# Revit family: QF_BPRO_HAU-PS 5x7_572556
name_source: partatom
category: Sonderausstattung
revit_build: Autodesk Revit 2018 (Build: 20190510_1515(x64)
units: mm (PartAtom-declared; Revit-internal decimal feet)

## family parameters
Arbeitsebenenbasiert = Nein
Beim Laden mit Abzugskörper schneiden = Nein
Bemaßung runder Anschluss = Durchmesser verwenden
Gemeinsam genutzt = Nein
Immer vertikal = Ja
Raumberechnungspunkt = Nein
Teiletyp = Normal

## types (1)
- HAU-PS 5x7
    Artikel Nummer = 572556
    Beschreibung = Handwasch- und Ausgussbecken-Kombination auf Füßen stehend, mit
abnehmbarer Serviceblende,
komplett mit 1 Mischbatterie 1/2" und einer sensorgesteuerten
Mischbatterie und Ablaufgarnitur
Maße: Handwaschbecken: 340 x 240 x 150 mm
Ausgussbecken: 370 x 340 x 150
    Beschreibung durch Hersteller analog Leistungsverzeichniskurztext = Abmessungen:

Länge:   	500 mm
Breite:  	700 mm
Höhe:          900/560 mm

Beckengröße:
Länge:   	340 mm
Breite:  	240 mm
Höhe:    	150 mm

Länge:   	370 mm
Breite:  	340 mm
Höhe:    	150 mm


Ausführung:

Handwasch- und Ausgussbecken sind aus platzsparenden Gründen übereinander angeordnet. Bestehend aus einer kompakten, selbsttragenden Bauweise, auf vier längsnahtgeschweißten Vierkantrohrfüßen (je 40x40x1,25 mm) stehend. Die Steherenden sind zum Ausgleich von Bodenunebenheiten mit höhenverstellbaren Kunststoffschraubstollen (+/- 15 mm) ausgestattet. 

Beide Becken sind mit dreiseitigen CNS-Blenden versehen, wobei die schräg angeordnete Verkleidung des Waschbeckens abnehmbar ist. Die Becken sind im Einstückverfahren tiefgezogen und naht- und fugenlos in die Abdeckung eingeschweißt. Die Abdeckungen sind dreiseitig 50 mm abgekantet. Das Handwaschbecken ist hinten 50 mm aufgekantet mit Umschlag nach außen. Das Ausgussbecken ist umlaufend mit einem erhöhten Profilrand (Schwallrand) versehen.

Die Handwasch-Ausgussbecken-Kombination ist mit Stopfen-Überlaufventilen 1 1/2" und mit einem Auflagerost aus stabilem Kunststoff (Material: ASA) ausgestattet. Das Handwaschbecken ist mit einer berührungslosen Armatur 1/2" (Modell Aquis) versehen. Die Temperatur ist mittels seitlich angeordnetem Hebel individuell von kalt bis warm einstellbar. Sobald die Hände unter die Armatur gehalten werden, fließt automatisch das Wasser in der vorgewählten Temperatur, bei Wegziehen stoppt der Wasserfluss automatisch. Der Trafo wird im Unterbereich mit Netzanschluss von 230 V/ 50 HZ und entsprechendem Anschlußkabel eingebaut. 
Die manuell regelbare Einhebel-Mischbatterie 1/2" für das Ausgussbecken ist ebenfalls zur Montage auf dem Handwaschbecken vorgesehen.
Die Ver- und Entsorgungsleitungen sowie die Armaturen sind lose beigefügt und können problem-los mittels einer Bedienungs- und Montageanleitung installiert werden. 


Zubehör/ Optionen:

<unrecoverable-encoding: 3 bytes ef82a7>	Abfallschublade:
Die Abfallschublade ist für alle Modelle HAU-P und 
HAU-PS erhältlich. Sie ist unterhalb des 
Ausgussbeckens platziert und lässt sich per Fuß 
öffnen und schließen. Als Abfallbehälter dient ein 
B.PRO
    Beschreibung durch Hersteller analog Leistungsverzeichnislangtext = Abmessungen:

Länge:   	500 mm
Breite:  	700 mm
Höhe:          900/560 mm

Beckengröße:
Länge:   	340 mm
Breite:  	240 mm
Höhe:    	150 mm

Länge:   	370 mm
Breite:  	340 mm
Höhe:    	150 mm


Ausführung:

Handwasch- und Ausgussbecken sind aus platzsparenden Gründen übereinander angeordnet. Bestehend aus einer kompakten, selbsttragenden Bauweise, auf vier längsnahtgeschweißten Vierkantrohrfüßen (je 40x40x1,25 mm) stehend. Die Steherenden sind zum Ausgleich von Bodenunebenheiten mit höhenverstellbaren Kunststoffschraubstollen (+/- 15 mm) ausgestattet. 

Beide Becken sind mit dreiseitigen CNS-Blenden versehen, wobei die schräg angeordnete Verkleidung des Waschbeckens abnehmbar ist. Die Becken sind im Einstückverfahren tiefgezogen und naht- und fugenlos in die Abdeckung eingeschweißt. Die Abdeckungen sind dreiseitig 50 mm abgekantet. Das Handwaschbecken ist hinten 50 mm aufgekantet mit Umschlag nach außen. Das Ausgussbecken ist umlaufend mit einem erhöhten Profilrand (Schwallrand) versehen.

Die Handwasch-Ausgussbecken-Kombination ist mit Stopfen-Überlaufventilen 1 1/2" und mit einem Auflagerost aus stabilem Kunststoff (Material: ASA) ausgestattet. Das Handwaschbecken ist mit einer berührungslosen Armatur 1/2" (Modell Aquis) versehen. Die Temperatur ist mittels seitlich angeordnetem Hebel individuell von kalt bis warm einstellbar. Sobald die Hände unter die Armatur gehalten werden, fließt automatisch das Wasser in der vorgewählten Temperatur, bei Wegziehen stoppt der Wasserfluss automatisch. Der Trafo wird im Unterbereich mit Netzanschluss von 230 V/ 50 HZ und entsprechendem Anschlußkabel eingebaut. 
Die manuell regelbare Einhebel-Mischbatterie 1/2" für das Ausgussbecken ist ebenfalls zur Montage auf dem Handwaschbecken vorgesehen.
Die Ver- und Entsorgungsleitungen sowie die Armaturen sind lose beigefügt und können problem-los mittels einer Bedienungs- und Montageanleitung installiert werden. 


Zubehör/ Optionen:

<unrecoverable-encoding: 3 bytes ef82a7>	Abfallschublade:
Die Abfallschublade ist für alle Modelle HAU-P und 
HAU-PS erhältlich. Sie ist unterhalb des 
Ausgussbeckens platziert und lässt sich per Fuß 
öffnen und schließen. Als Abfallbehälter dient ein 
B.PRO
    Breite Becken unten Strg = 339 mm
    Frequenz = 50 Hz
    Gerätegewicht Netto = 23.00 kg
    Großküchengerätezuordnung = Ja
    Hauptschalter integriert = Nein
    Hersteller = B.PRO GmbH
    Höhe = 900 mm  [stored 2.95276 ft]
    Höhe Becken oben = 150 mm  [stored 0.492126 ft]
    Höhe Becken unten = 150 mm  [stored 0.492126 ft]
    Höhe Becken1 = 610 mm  [stored 2.00131 ft]
    Internetadresse Gerätehersteller = https://www.bpro-solutions.com
    Internetadresse für Ersatzteilliste = https://www.bpro-solutions.com
    Korpus UK = 330 mm
    Kosten = 1594.5 $
    Länge Becken oben = 340 mm
    Länge Becken unten = 370 mm  [stored 1.21391 ft]
    Länge Gerätebreite = 500 mm  [stored 1.64042 ft]
    Material = QF_Metal-Stainless-Steel_general
    Material Füße = QF_Plastic-Dark_Grey-Matt
    Modell = HAU-PS 5x7
    Sockelhöhe = 34 mm  [stored 0.111549 ft]
    Spannung = 240 V
    Tiefe = 700 mm  [stored 2.29659 ft]
    Tiefe Becken oben = 240 mm  [stored 0.787402 ft]
    Tiefe Becken unten = 340 mm
    Tiefe oben = 320 mm  [stored 1.04987 ft]
    Typenkommentare = Handwasch- und Ausgussbecken-Kombination, stehend, mit abnehmbarer Serviceblende
    URL = https://www.bpro-solutions.com
    Warnhinweise = Ausführliche Gefahrenhinweise entnehmen Sie der Betriebsanleitung.
    Zubehör = Nein

note: [stored X ft] marks values corroborated as IEEE doubles in the binary element streams (Revit-internal decimal feet)

## geometry (parser evidence)
native form markers: Blend x4
no freeform markers — native parametric forms only
